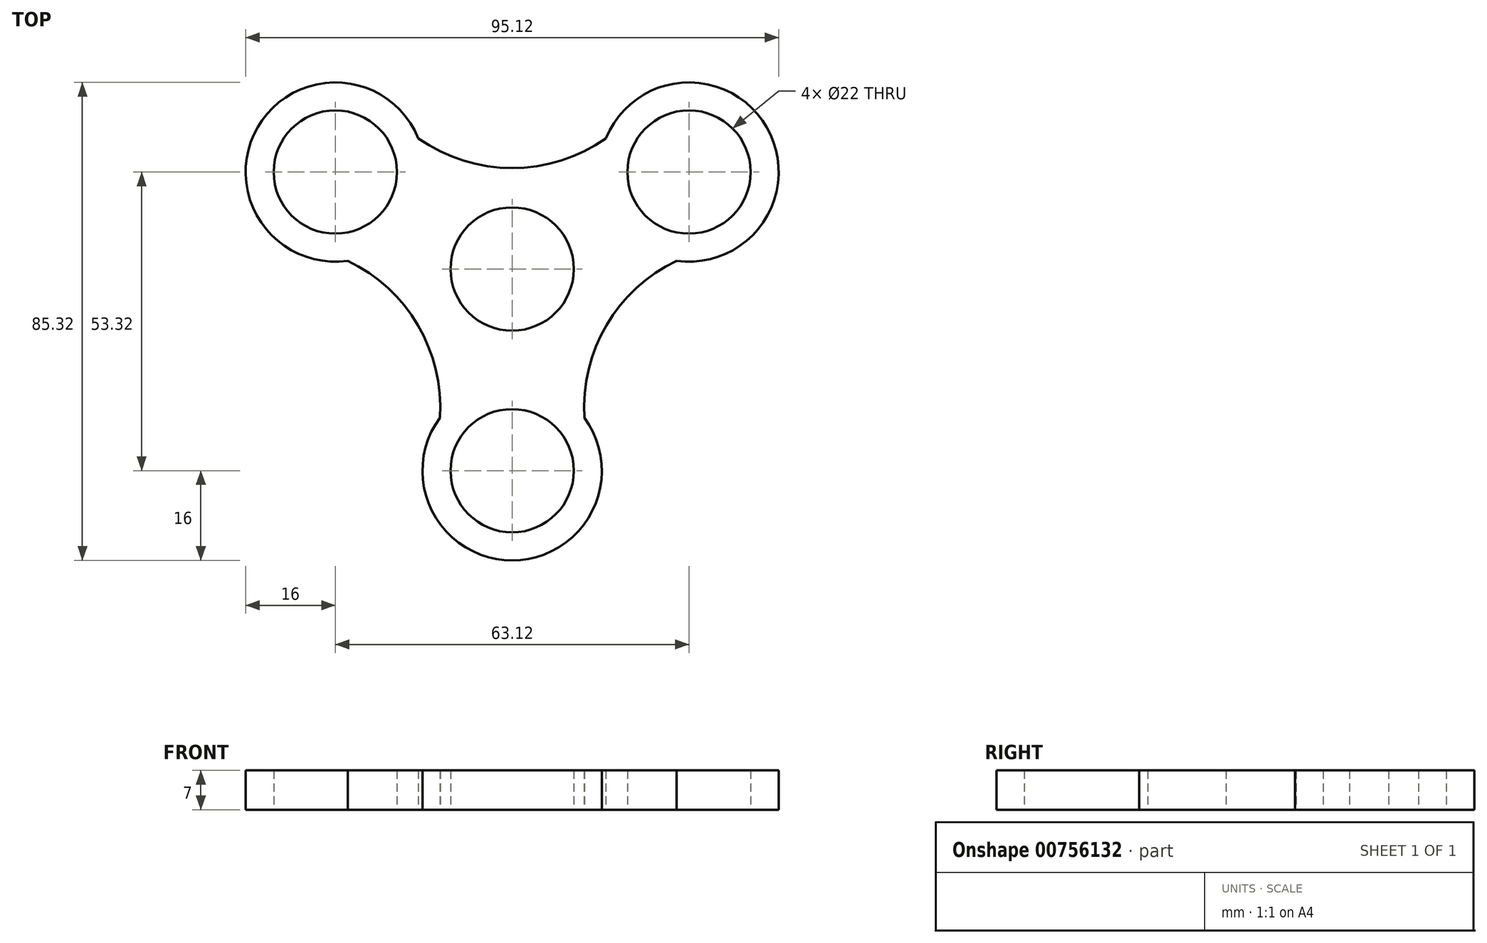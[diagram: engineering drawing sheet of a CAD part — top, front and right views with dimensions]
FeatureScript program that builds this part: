
annotation { "Feature Type Name" : "Feature", "Feature Type Description" : "" }
export const myFeature = defineFeature(function(context is Context, id is Id, definition is map)
    precondition{}
    {
        {
            var Q0;
            Q0=qCreatedBy(makeId("Top.planeOp"),FACE);
            var sketch = newSketch(context, id + "F0", { "sketchPlane" : qUnion([Q0])});
            skCircle(sketch, "E0", {"center": v(0, 0) * mm, "radius": 11 * mm});
            skCircle(sketch, "E1", {"center": v(-31.56, 17.32) * mm, "radius": 11 * mm});
            skCircle(sketch, "E2", {"center": v(31.56, 17.32) * mm, "radius": 11 * mm});
            skCircle(sketch, "E3", {"center": v(0, -36) * mm, "radius": 11 * mm});
            skLineSegment(sketch, "E4", {"start": v(0, 0) * mm, "end": v(0, -68.66) * mm, "construction": true});
            skCircle(sketch, "E5", {"center": v(31.56, 17.32) * mm, "radius": 16 * mm});
            skCircle(sketch, "E6", {"center": v(-31.56, 17.32) * mm, "radius": 16 * mm});
            skCircle(sketch, "E7", {"center": v(0, -36) * mm, "radius": 16 * mm});
            skLineSegment(sketch, "E8", {"start": v(-38.13, 2.73) * mm, "end": v(-31.56, 17.32) * mm, "construction": true});
            skLineSegment(sketch, "E9", {"start": v(-31.56, 17.32) * mm, "end": v(-24.99, 31.9) * mm, "construction": true});
            skPoint(sketch, "E10.orphan", {"position": v(24.99, 31.9) * mm});
            skLineSegment(sketch, "E11", {"start": v(38.13, 2.73) * mm, "end": v(31.56, 17.32) * mm, "construction": true});
            skLineSegment(sketch, "E12", {"start": v(31.56, 17.32) * mm, "end": v(24.99, 31.9) * mm, "construction": true});
            skLineSegment(sketch, "E13.trimOffspring", {"start": v(-38.13, 2.73) * mm, "end": v(-80.4, 3.52) * mm});
            skArc(sketch, "E14", {"start": v(29.35, 1.47) * mm, "mid": v(16.84, -10) * mm, "end": v(12.9, -26.53) * mm});
            skArc(sketch, "E15", {"start": v(-12.9, -26.53) * mm, "mid": v(-16.84, -10) * mm, "end": v(-29.35, 1.47) * mm});
            skLineSegment(sketch, "E16", {"start": v(29.35, 1.47) * mm, "end": v(-64.15, 1.47) * mm, "construction": true});
            skLineSegment(sketch, "E17", {"start": v(-29.35, 1.47) * mm, "end": v(0, 52.3) * mm, "construction": true});
            skLineSegment(sketch, "E18", {"start": v(0, 52.3) * mm, "end": v(29.35, 1.47) * mm, "construction": true});
            skArc(sketch, "E19", {"start": v(-16.73, 23.33) * mm, "mid": v(0, 18.02) * mm, "end": v(16.73, 23.33) * mm});
            skLineSegment(sketch, "E20", {"start": v(-16.73, 23.33) * mm, "end": v(16.73, 23.33) * mm, "construction": true});
            skSolve(sketch);
        }
        {
            var Q0;
            {var subQ0=sQuery(id+"F0.wireOp",EDGE,"0TSceduz-cEnI-4jYJ-D3ID-3SMpwCBie2t2");Q0=makeQuery(id+"F0.imprint","IMPRINT",FACE,{"disambiguationData":[TD([[makeQuery(id+"F0.imprint","IMPRINT",EDGE,{"derivedFrom":subQ0}),-1.0]])]});}
            var Q1;
            {var subQ0=sQuery(id+"F0.wireOp",EDGE,"e62Aefh6-yg1u-UyLL-kMEe-4k4CW6gHobVo");Q1=makeQuery(id+"F0.imprint","IMPRINT",FACE,{"disambiguationData":[TD([[makeQuery(id+"F0.imprint","IMPRINT",EDGE,{"derivedFrom":subQ0}),-1.0]])]});}
            var Q2;
            Q2=makeQuery(id+"F0.imprint","IMPRINT",FACE,{"disambiguationData":[TD([[makeQuery(id+"F0.imprint","IMPRINT",EDGE,{"derivedFrom":sQuery(id+"F0.wireOp",EDGE,"E0")}),-1.0]])]});
            extrude(context, id + "F1", {"entities" : qUnion([Q0, Q1, Q2]), "depth" : 7 * mm, "offsetDistance" : 25 * mm});
        }
        {
            var Q0;
            Q0=makeQuery(id+"F0.imprint","IMPRINT",FACE,{"disambiguationData":[TD([[makeQuery(id+"F0.imprint","IMPRINT",EDGE,{"derivedFrom":sQuery(id+"F0.wireOp",EDGE,"E2")}),-1.0]])]});
            var Q1;
            Q1=makeQuery(id+"F0.imprint","IMPRINT",FACE,{"disambiguationData":[TD([[makeQuery(id+"F0.imprint","IMPRINT",EDGE,{"derivedFrom":sQuery(id+"F0.wireOp",EDGE,"E1")}),-1.0]])]});
            var Q2;
            Q2=makeQuery(id+"F0.imprint","IMPRINT",FACE,{"disambiguationData":[TD([[makeQuery(id+"F0.imprint","IMPRINT",EDGE,{"derivedFrom":sQuery(id+"F0.wireOp",EDGE,"E3")}),-1.0]])]});
            extrude(context, id + "F2", {"entities" : qUnion([Q0, Q1, Q2]), "operationType" : NewBodyOperationType.ADD, "depth" : 7 * mm, "offsetDistance" : 25 * mm});
        }
    });
